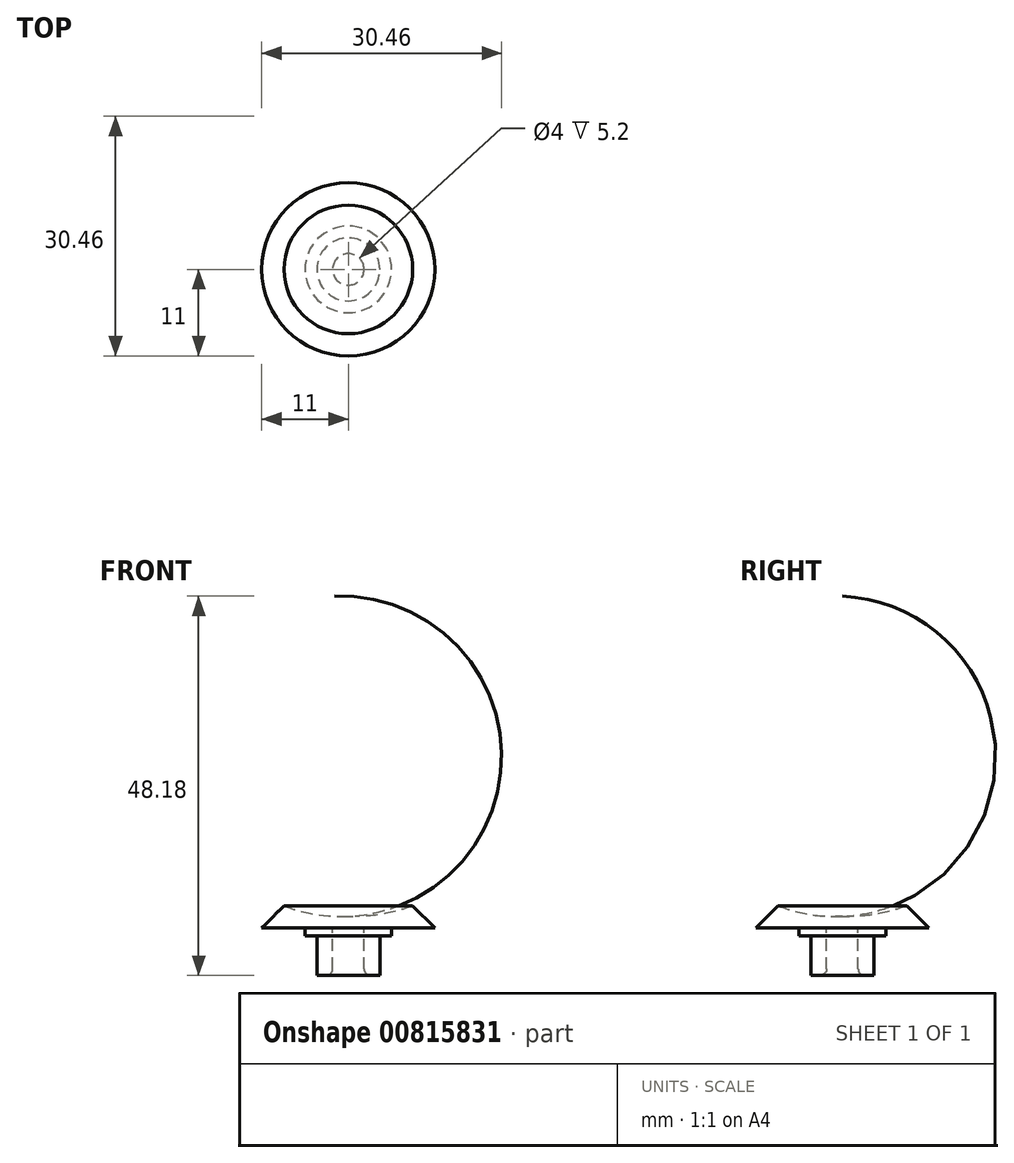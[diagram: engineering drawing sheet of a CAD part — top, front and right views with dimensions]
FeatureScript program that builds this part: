
annotation { "Feature Type Name" : "Feature", "Feature Type Description" : "" }
export const myFeature = defineFeature(function(context is Context, id is Id, definition is map)
    precondition{}
    {
        {
            var Q0;
            Q0=qCreatedBy(makeId("Front.planeOp"),FACE);
            var sketch = newSketch(context, id + "F0", { "sketchPlane" : qUnion([Q0])});
            skLineSegment(sketch, "E0", {"start": v(0, 0) * mm, "end": v(-11, 0) * mm});
            skLineSegment(sketch, "E1", {"start": v(-11, 0) * mm, "end": v(-8.17, 2.83) * mm});
            skLineSegment(sketch, "E2", {"start": v(0, 0) * mm, "end": v(0, 1.5) * mm});
            skArc(sketch, "E3", {"start": v(-8.17, 2.83) * mm, "mid": v(-4.15, 1.74) * mm, "end": v(0, 1.5) * mm});
            skSolve(sketch);
        }
        {
            var Q0;
            Q0=makeQuery(id+"F0.imprint","IMPRINT",FACE,{"disambiguationData":[TD([[makeQuery(id+"F0.imprint","IMPRINT",EDGE,{"derivedFrom":sQuery(id+"F0.wireOp",EDGE,"E0")}),-1.0]])]});
            var Q1;
            Q1=sQuery(id+"F0.wireOp",EDGE,"E2");
            revolve(context, id + "F1", {"surfaceOperationType" : NewSurfaceOperationType.NEW, "entities" : qUnion([Q0]), "axis" : qUnion([Q1]), "revolveType" : RevolveType.FULL});
        }
        {
            var Q0;
            Q0=makeQuery(id+"F1.opRevolve","SWEPT_FACE",FACE,{"disambiguationData":[OSD([sQuery(id+"F0.wireOp",EDGE,"E0")])]});
            var sketch = newSketch(context, id + "F2", { "sketchPlane" : qUnion([Q0])});
            skCircle(sketch, "E4", {"center": v(0, 0) * mm, "radius": 5.5 * mm});
            skCircle(sketch, "E5", {"center": v(0, 0) * mm, "radius": 4 * mm});
            skCircle(sketch, "E6", {"center": v(0, 0) * mm, "radius": 2 * mm});
            skSolve(sketch);
        }
        {
            var Q0;
            Q0=makeQuery(id+"F2.imprint","IMPRINT",FACE,{"disambiguationData":[TD([[makeQuery(id+"F2.imprint","IMPRINT",EDGE,{"derivedFrom":sQuery(id+"F2.wireOp",EDGE,"E4")}),1.0]])]});
            extrude(context, id + "F3", {"entities" : qUnion([Q0]), "operationType" : NewBodyOperationType.ADD, "depth" : 1 * mm, "offsetDistance" : 25 * mm});
        }
        {
            var Q0;
            Q0=makeQuery(id+"F2.imprint","IMPRINT",FACE,{"disambiguationData":[TD([[makeQuery(id+"F2.imprint","IMPRINT",EDGE,{"derivedFrom":sQuery(id+"F2.wireOp",EDGE,"E5")}),1.0]])]});
            extrude(context, id + "F4", {"entities" : qUnion([Q0]), "operationType" : NewBodyOperationType.ADD, "depth" : 6 * mm, "offsetDistance" : 25 * mm});
        }
        {
            var Q0;
            Q0=makeQuery(id+"F4.opExtrude","CAP_EDGE",EDGE,{"disambiguationData":[OSD([sQuery(id+"F2.wireOp",EDGE,"E6")])],"isStart":false});
            fillet(context, id + "F5", {"entities" : qUnion([Q0]), "radius" : .8 * mm, "tangentPropagation" : true, "allowEdgeOverflow" : false});
        }
    });
